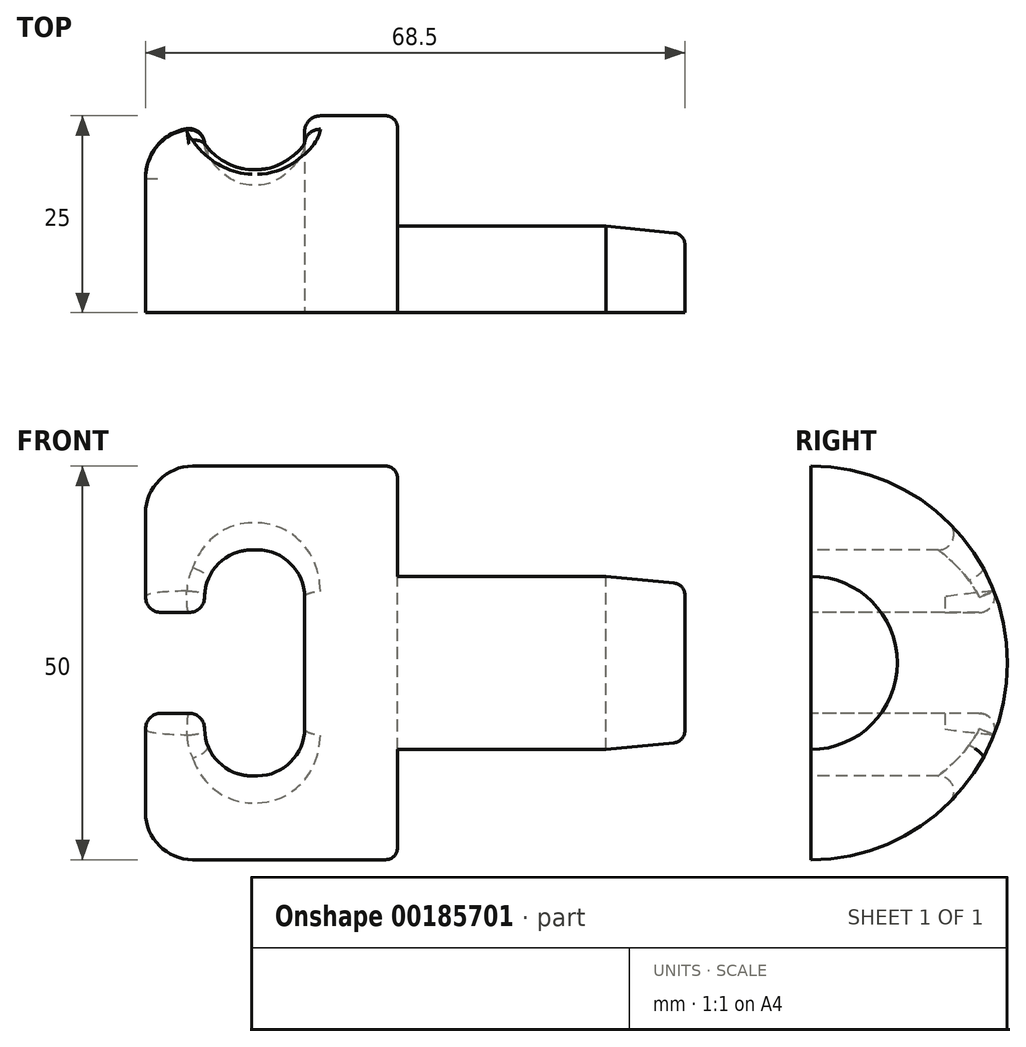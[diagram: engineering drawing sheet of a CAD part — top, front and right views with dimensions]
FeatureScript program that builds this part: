
annotation { "Feature Type Name" : "Feature", "Feature Type Description" : "" }
export const myFeature = defineFeature(function(context is Context, id is Id, definition is map)
    precondition{}
    {
        {
            var Q0;
            Q0=qCreatedBy(makeId("Right.planeOp"),FACE);
            var sketch = newSketch(context, id + "F0", { "sketchPlane" : qUnion([Q0])});
            skCircle(sketch, "E0", {"center": v(0, 0) * mm, "radius": 11 * mm});
            skSolve(sketch);
        }
        {
            var Q0;
            Q0 = qSketchRegion(id + "F0", true);
            extrude(context, id + "F1", {"entities" : qUnion([Q0]), "depth" : 36.5 * mm});
        }
        {
            var Q0;
            Q0=makeQuery(id+"F1.opExtrude","CAP_EDGE",EDGE,{"disambiguationData":[OSD([sQuery(id+"F0.wireOp",EDGE,"E0")])],"isStart":false});
            chamfer(context, id + "F2", {"entities" : qUnion([Q0]), "chamferType" : ChamferType.TWO_OFFSETS, "width1" : 1 * mm, "oppositeDirection" : false, "width2" : 10 * mm, "tangentPropagation" : true});
        }
        {
            var Q0;
            Q0=qCreatedBy(makeId("Right.planeOp"),FACE);
            var sketch = newSketch(context, id + "F3", { "sketchPlane" : qUnion([Q0])});
            skCircle(sketch, "E1", {"center": v(0, 0) * mm, "radius": 25 * mm});
            skSolve(sketch);
        }
        {
            var Q0;
            Q0 = qSketchRegion(id + "F3", true);
            extrude(context, id + "F4", {"entities" : qUnion([Q0]), "operationType" : NewBodyOperationType.ADD, "oppositeDirection" : true, "depth" : 32 * mm});
        }
        {
            var Q0;
            Q0=qCreatedBy(makeId("Front.planeOp"),FACE);
            cPlane(context, id + "F5", {"entities" : qUnion([Q0]), "cplaneType" : CPlaneType.OFFSET, "offset" : 25 * mm, "width" : 150 * mm, "height" : 150 * mm});
        }
        {
            var Q0;
            Q0=qCreatedBy(id+"F5.planeOp",FACE);
            var sketch = newSketch(context, id + "F6", { "sketchPlane" : qUnion([Q0])});
            skLineSegment(sketch, "E2.bottom", {"start": v(-11.8, -14.35) * mm, "end": v(-24.5, -14.35) * mm});
            skLineSegment(sketch, "E2.top", {"start": v(-11.8, 14.35) * mm, "end": v(-24.5, 14.35) * mm});
            skLineSegment(sketch, "E2.left", {"start": v(-11.8, -14.35) * mm, "end": v(-11.8, 14.35) * mm});
            skLineSegment(sketch, "E2.right", {"start": v(-24.5, -14.35) * mm, "end": v(-24.5, 14.35) * mm});
            skPoint(sketch, "E2.middle", {"position": v(-18.15, 0) * mm});
            skLineSegment(sketch, "E3.bottom", {"start": v(-24.5, 6.4) * mm, "end": v(-32, 6.4) * mm});
            skLineSegment(sketch, "E3.top", {"start": v(-24.5, -6.4) * mm, "end": v(-32, -6.4) * mm});
            skLineSegment(sketch, "E3.left", {"start": v(-24.5, 6.4) * mm, "end": v(-24.5, -6.4) * mm});
            skLineSegment(sketch, "E3.right", {"start": v(-32, 6.4) * mm, "end": v(-32, -6.4) * mm});
            skPoint(sketch, "E3.middle", {"position": v(-28.25, 0) * mm});
            skSolve(sketch);
        }
        {
            var Q0;
            Q0 = qSketchRegion(id + "F6", true);
            extrude(context, id + "F7", {"entities" : qUnion([Q0]), "operationType" : NewBodyOperationType.REMOVE, "endBound" : BoundingType.THROUGH_ALL, "oppositeDirection" : true, "depth" : 25 * mm});
        }
        {
            var Q0;
            {var subQ0=sQuery(id+"F3.wireOp",EDGE,"E1");Q0=makeQuery(id+"F7.boolean.opBoolean","SPLIT",EDGE,{"disambiguationData":[TD([makeQuery(id+"F7.opExtrude","SWEPT_FACE",FACE,{"disambiguationData":[OSD([sQuery(id+"F6.wireOp",EDGE,"E3.bottom")])]})])],"derivedFrom":makeQuery(id+"F4.opExtrude","CAP_EDGE",EDGE,{"disambiguationData":[OSD([subQ0])],"isStart":false})});}
            var Q1;
            Q1=makeQuery(id+"F7.boolean.opBoolean","COPY",EDGE,{"derivedFrom":makeQuery(id+"F7.opExtrude","SWEPT_EDGE",EDGE,{"disambiguationData":[OSD([sQuery(id+"F6.wireOp",EDGE,"E2.top"),sQuery(id+"F6.wireOp",EDGE,"E2.left")])]})});
            var Q2;
            Q2=makeQuery(id+"F7.boolean.opBoolean","COPY",EDGE,{"derivedFrom":makeQuery(id+"F7.opExtrude","SWEPT_EDGE",EDGE,{"disambiguationData":[OSD([sQuery(id+"F6.wireOp",EDGE,"E2.top"),sQuery(id+"F6.wireOp",EDGE,"E2.right")])]})});
            var Q3;
            {var subQ0=sQuery(id+"F3.wireOp",EDGE,"E1");Q3=makeQuery(id+"F7.boolean.opBoolean","SPLIT",EDGE,{"disambiguationData":[TD([makeQuery(id+"F7.opExtrude","SWEPT_FACE",FACE,{"disambiguationData":[OSD([sQuery(id+"F6.wireOp",EDGE,"E3.top")])]})])],"derivedFrom":makeQuery(id+"F4.opExtrude","CAP_EDGE",EDGE,{"disambiguationData":[OSD([subQ0])],"isStart":false})});}
            var Q4;
            Q4=makeQuery(id+"F7.boolean.opBoolean","COPY",EDGE,{"derivedFrom":makeQuery(id+"F7.opExtrude","SWEPT_EDGE",EDGE,{"disambiguationData":[OSD([sQuery(id+"F6.wireOp",EDGE,"E2.bottom"),sQuery(id+"F6.wireOp",EDGE,"E2.left")])]})});
            var Q5;
            Q5=makeQuery(id+"F7.boolean.opBoolean","COPY",EDGE,{"derivedFrom":makeQuery(id+"F7.opExtrude","SWEPT_EDGE",EDGE,{"disambiguationData":[OSD([sQuery(id+"F6.wireOp",EDGE,"E2.bottom"),sQuery(id+"F6.wireOp",EDGE,"E2.right")])]})});
            fillet(context, id + "F8", {"entities" : qUnion([Q0, Q1, Q2, Q3, Q4, Q5]), "radius" : 6 * mm, "tangentPropagation" : true, "allowEdgeOverflow" : false});
        }
        {
            var Q0;
            {var subQ0=makeQuery(id+"F7.opExtrude","SWEPT_FACE",FACE,{"disambiguationData":[OSD([sQuery(id+"F6.wireOp",EDGE,"E3.top")])]});var subQ1=sQuery(id+"F3.wireOp",EDGE,"E1");Q0=makeQuery(id+"F8.opFillet","BLEND_EDGE",EDGE,{"disambiguationData":[OD(0.0)],"blendedFrom":[makeQuery(id+"F7.boolean.opBoolean","SPLIT",EDGE,{"disambiguationData":[TD([subQ0])],"derivedFrom":makeQuery(id+"F4.opExtrude","CAP_EDGE",EDGE,{"disambiguationData":[OSD([subQ1])],"isStart":false})}),makeQuery(id+"F7.boolean.opBoolean","COPY",FACE,{"derivedFrom":subQ0})],"blendedInto":[makeQuery(id+"F7.boolean.opBoolean","COPY",FACE,{"derivedFrom":subQ0})]});}
            var Q1;
            {var subQ0=makeQuery(id+"F7.opExtrude","SWEPT_FACE",FACE,{"disambiguationData":[OSD([sQuery(id+"F6.wireOp",EDGE,"E3.bottom")])]});var subQ1=sQuery(id+"F3.wireOp",EDGE,"E1");Q1=makeQuery(id+"F8.opFillet","BLEND_EDGE",EDGE,{"disambiguationData":[OD(0.0)],"blendedFrom":[makeQuery(id+"F7.boolean.opBoolean","SPLIT",EDGE,{"disambiguationData":[TD([subQ0])],"derivedFrom":makeQuery(id+"F4.opExtrude","CAP_EDGE",EDGE,{"disambiguationData":[OSD([subQ1])],"isStart":false})}),makeQuery(id+"F7.boolean.opBoolean","COPY",FACE,{"derivedFrom":subQ0})],"blendedInto":[makeQuery(id+"F7.boolean.opBoolean","COPY",FACE,{"derivedFrom":subQ0})]});}
            var Q2;
            Q2=makeQuery(id+"F7.boolean.opBoolean","INTERSECT",EDGE,{"disambiguationData":[OD(1.0)],"derivedFrom":[makeQuery(id+"F4.opExtrude","SWEPT_FACE",FACE,{"disambiguationData":[OSD([sQuery(id+"F3.wireOp",EDGE,"E1")])]}),makeQuery(id+"F7.opExtrude","SWEPT_FACE",FACE,{"disambiguationData":[OSD([sQuery(id+"F6.wireOp",EDGE,"E2.left")])]})]});
            var Q3;
            Q3=makeQuery(id+"F7.boolean.opBoolean","INTERSECT",EDGE,{"disambiguationData":[OD(0.0)],"derivedFrom":[makeQuery(id+"F4.opExtrude","SWEPT_FACE",FACE,{"disambiguationData":[OSD([sQuery(id+"F3.wireOp",EDGE,"E1")])]}),makeQuery(id+"F7.opExtrude","SWEPT_FACE",FACE,{"disambiguationData":[OSD([sQuery(id+"F6.wireOp",EDGE,"E2.left")])]})]});
            fillet(context, id + "F9", {"entities" : qUnion([Q0, Q1, Q2, Q3]), "radius" : 2 * mm, "tangentPropagation" : true, "allowEdgeOverflow" : false});
        }
        {
            var Q0;
            {var subQ0=sQuery(id+"F0.wireOp",EDGE,"E0");Q0=makeQuery(id+"F2.opChamfer","BLEND_EDGE",EDGE,{"blendedFrom":[makeQuery(id+"F1.opExtrude","CAP_EDGE",EDGE,{"disambiguationData":[OSD([subQ0])],"isStart":false}),makeQuery(id+"F1.opExtrude","CAP_FACE",FACE,{"disambiguationData":[OSD([subQ0])],"isStart":false})],"blendedInto":[makeQuery(id+"F1.opExtrude","CAP_FACE",FACE,{"disambiguationData":[OSD([subQ0])],"isStart":false})]});}
            var Q1;
            Q1=makeQuery(id+"F4.opExtrude","CAP_EDGE",EDGE,{"disambiguationData":[OSD([sQuery(id+"F3.wireOp",EDGE,"E1")])],"isStart":true});
            fillet(context, id + "F10", {"entities" : qUnion([Q0, Q1]), "radius" : 1.5 * mm, "tangentPropagation" : true, "allowEdgeOverflow" : false});
        }
        {
            var Q0;
            Q0=makeQuery(id+"F7.boolean.opBoolean","COPY",EDGE,{"derivedFrom":makeQuery(id+"F7.opExtrude","SWEPT_EDGE",EDGE,{"disambiguationData":[OSD([sQuery(id+"F6.wireOp",EDGE,"E2.right"),sQuery(id+"F6.wireOp",EDGE,"E3.bottom"),sQuery(id+"F6.wireOp",EDGE,"E3.left")])]})});
            var Q1;
            Q1=makeQuery(id+"F7.boolean.opBoolean","COPY",EDGE,{"derivedFrom":makeQuery(id+"F7.opExtrude","SWEPT_EDGE",EDGE,{"disambiguationData":[OSD([sQuery(id+"F6.wireOp",EDGE,"E2.right"),sQuery(id+"F6.wireOp",EDGE,"E3.top"),sQuery(id+"F6.wireOp",EDGE,"E3.left")])]})});
            fillet(context, id + "F11", {"entities" : qUnion([Q0, Q1]), "radius" : 2 * mm, "tangentPropagation" : true, "allowEdgeOverflow" : false});
        }
        {
            var Q0;
            Q0=qCreatedBy(makeId("Right.planeOp"),FACE);
            var sketch = newSketch(context, id + "F12", { "sketchPlane" : qUnion([Q0])});
            skLineSegment(sketch, "E4.bottom", {"start": v(0, 30) * mm, "end": v(-26, 30) * mm});
            skLineSegment(sketch, "E4.top", {"start": v(0, -34.52) * mm, "end": v(-26, -34.52) * mm});
            skLineSegment(sketch, "E4.left", {"start": v(0, 30) * mm, "end": v(0, -34.52) * mm});
            skLineSegment(sketch, "E4.right", {"start": v(-26, 30) * mm, "end": v(-26, -34.52) * mm});
            skSolve(sketch);
        }
        {
            var Q0;
            Q0 = qSketchRegion(id + "F12", true);
            extrude(context, id + "F13", {"entities" : qUnion([Q0]), "operationType" : NewBodyOperationType.REMOVE, "endBound" : BoundingType.SYMMETRIC, "depth" : 74 * mm});
        }
    });
